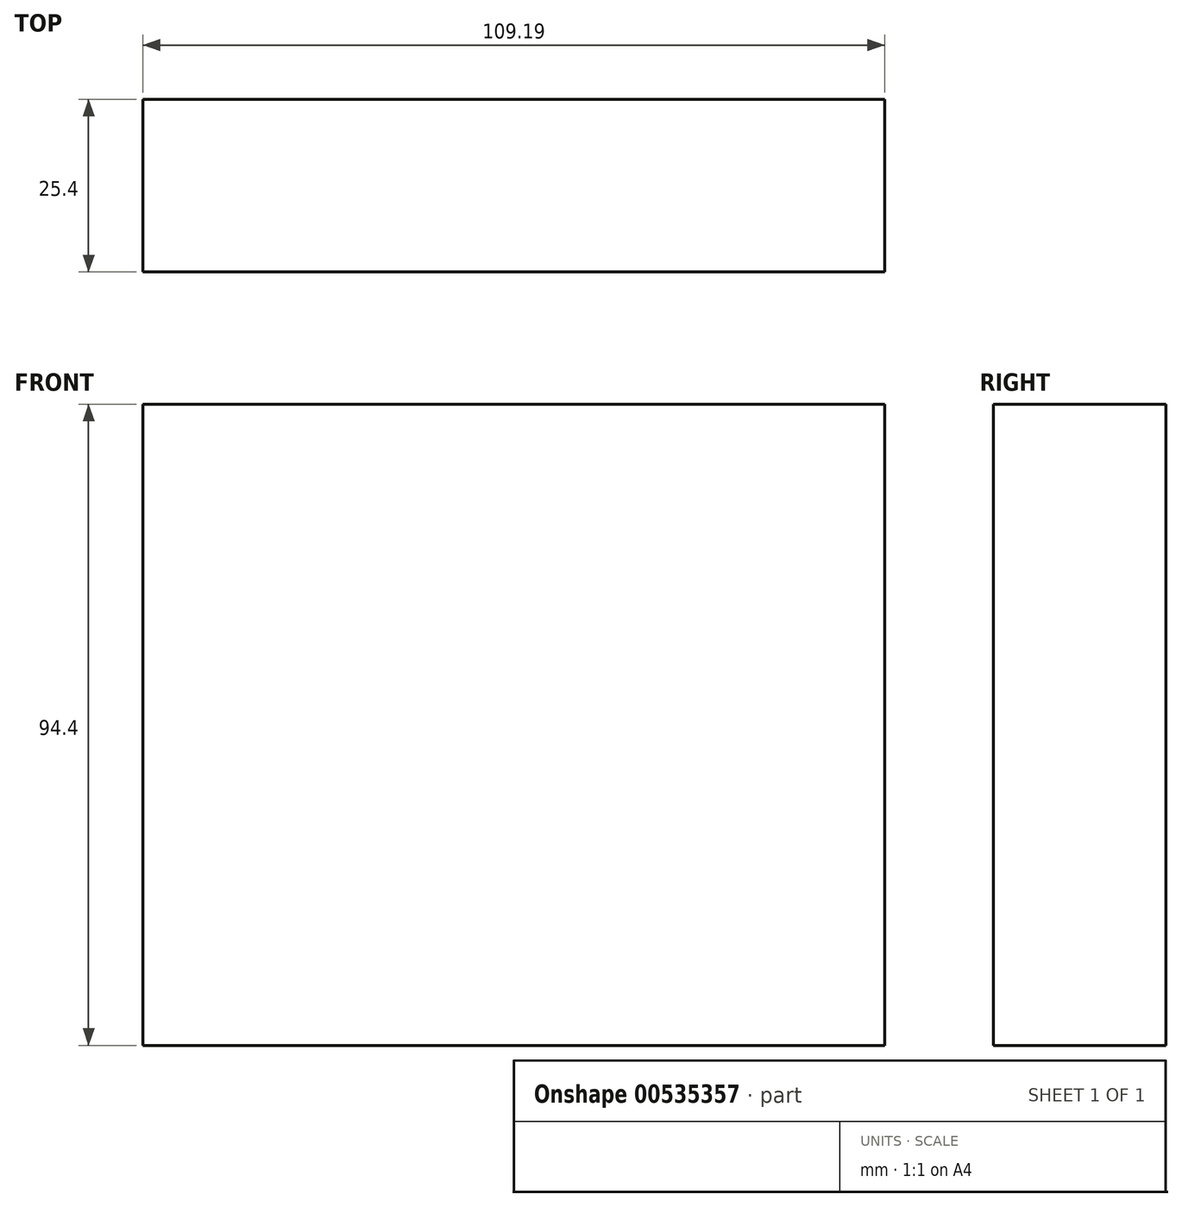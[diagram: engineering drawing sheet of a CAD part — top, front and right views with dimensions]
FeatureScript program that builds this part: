
annotation { "Feature Type Name" : "Feature", "Feature Type Description" : "" }
export const myFeature = defineFeature(function(context is Context, id is Id, definition is map)
    precondition{}
    {
        {
            var Q0;
            Q0=qCreatedBy(makeId("Front.planeOp"),FACE);
            var sketch = newSketch(context, id + "F0", { "sketchPlane" : qUnion([Q0])});
            skLineSegment(sketch, "E0.bottom", {"start": v(-50.76, 47.55) * mm, "end": v(58.43, 47.55) * mm});
            skLineSegment(sketch, "E0.top", {"start": v(-50.76, -46.85) * mm, "end": v(58.43, -46.85) * mm});
            skLineSegment(sketch, "E0.left", {"start": v(-50.76, 47.55) * mm, "end": v(-50.76, -46.85) * mm});
            skLineSegment(sketch, "E0.right", {"start": v(58.43, 47.55) * mm, "end": v(58.43, -46.85) * mm});
            skSolve(sketch);
        }
        {
            var Q0;
            Q0=makeQuery(id+"F0.imprint","IMPRINT",FACE,{"disambiguationData":[TD([[makeQuery(id+"F0.imprint","IMPRINT",EDGE,{"derivedFrom":sQuery(id+"F0.wireOp",EDGE,"E0.bottom")}),-1.0]])]});
            extrude(context, id + "F1", {"entities" : qUnion([Q0]), "depth" : 25.4 * mm, "offsetDistance" : 25.4 * mm});
        }
    });
